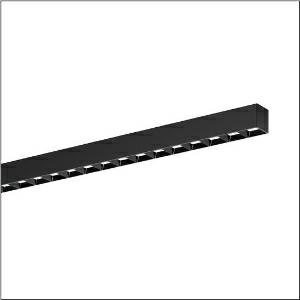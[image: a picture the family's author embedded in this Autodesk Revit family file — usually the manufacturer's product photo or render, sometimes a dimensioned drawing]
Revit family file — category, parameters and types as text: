
# Revit family: silica_r__21_51mx24dc3abb_157e
name_source: partatom
category: Lighting Fixtures
units: mm (PartAtom-declared; Revit-internal decimal feet)

## family parameters
Cut with Voids When Loaded = No
Host = Face
Light Source = No
Part Type = Normal
Room Calculation Point = No
Round Connector Dimension = Use Diameter
Shared = No

## types (1)
- --- (1 x LED, 10800 lm, 79 W, 3000K)
    Apparent Load = 79 VA
    CIE Flux Codes = 74 94 99 100 100
    Color Rendering = 80
    Color Temperature = 3000K
    Default Elevation = 1800 mm
    Description = Silica® 21, office luminaire, primary light control with darklight reflector, of PMMA, black, CAT 2 (L<= 3000cd/m²), light emission: direct distribution, primary light characteristic: asymmetric, installation type: surface-mounted, LED, rated luminous flux: 10.800lm, luminous efficacy: 137lm/W, light colour: 830, colour temperature: 3000K, control gear: DALI 2, with terminal, 3+2-pole, max. 2.5mm², mains connection: 220..240V, AC, 50/60Hz, rated input power: 79W, luminaire housing, of aluminium, matt jet black (RAL 9005), length: 3.004mm, width: 53mm, height: 53mm, protection rating (complete): IP20, insulation class (complete): insulation class I (protective earthing), certification: CE, permissible operating ambient temperature: 0..+35°C, standard: EN 50419, packaging unit: 1 piece
    Height = 53 mm
    Lamp = 1 x LED
    Lamp Light Flux = 10800 lm
    Lamp Power = 79 W
    Lamp count = 1
    Length = 3004 mm
    Luminous efficacy = 137 lm/W
    Manufacturer = Siteco
    ModVariant = No
    Model = 51MX24DC3ABB
    Mounting Place = Ceiling
    Mounting Type = Surface mounted
    Number of Poles = 1
    OnlyDefault = Yes
    Power Factor = 1
    Product Name = Silica® 21
    Product group = office luminaire | ceiling mounted
    ProductGroupID = 302
    Protection Class = Protection class I
    Protection Degree = IP 20
    RLX_Detail_Level = 1
    RLX_Emergency_Light_Flux = 0 lm
    RLX_Emergency_Type = 0
    RLX_Emergency_Type_DB = No
    RlxData = <blob elided: 64541 chars, md5=e633562b>
    Socket = socket
    Standby Power = 0 W
    System Light Flux = 10800 lm
    System Power = 79 W
    Type Comments = factory setting: luminous flux: 100 % | dim-lin: 254 | 448 mA
    Type Image = l_1335908.jpg
    URL = http://relux.com
    VarID = @adj_122824
    Voltage = 0 V
    Weight = 0.00 kg
    Width = 53 mm

## geometry (parser evidence)
native form markers: Blend x4, Sweep x9
no freeform markers — native parametric forms only
